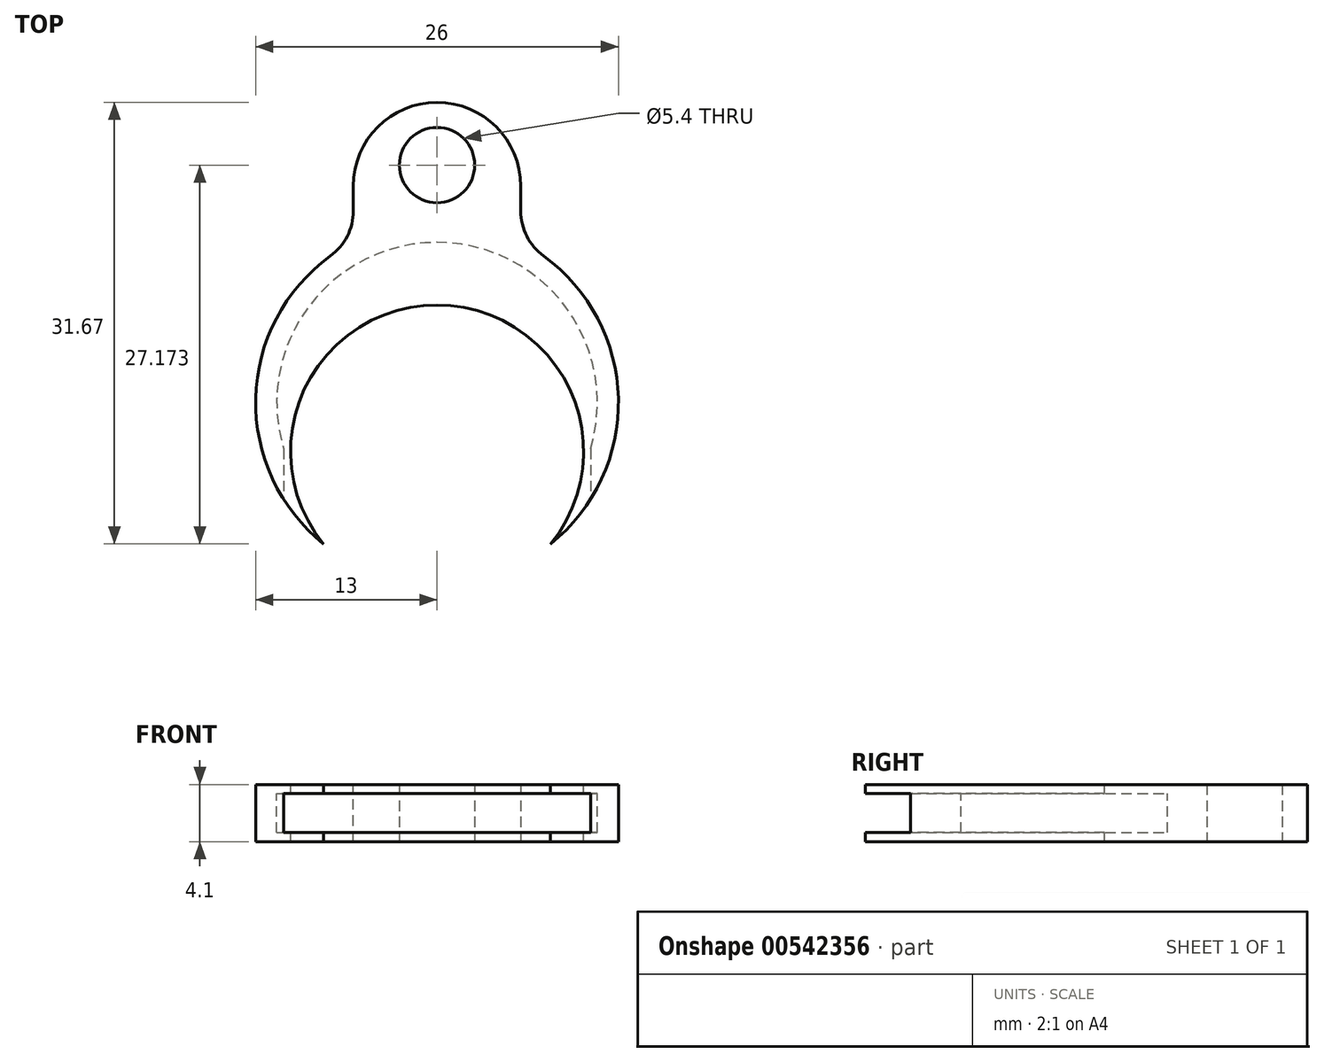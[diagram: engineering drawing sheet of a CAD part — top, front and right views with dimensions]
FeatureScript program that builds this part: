
annotation { "Feature Type Name" : "Feature", "Feature Type Description" : "" }
export const myFeature = defineFeature(function(context is Context, id is Id, definition is map)
    precondition{}
    {
        {
            var Q0;
            Q0=qCreatedBy(makeId("Top.planeOp"),FACE);
            var sketch = newSketch(context, id + "F0", { "sketchPlane" : qUnion([Q0])});
            skCircle(sketch, "E0", {"center": v(0, 0) * mm, "radius": 13 * mm});
            skLineSegment(sketch, "E1.bottom", {"start": v(-6, 21.53) * mm, "end": v(6, 21.53) * mm});
            skLineSegment(sketch, "E1.top", {"start": v(-6, 11.53) * mm, "end": v(6, 11.53) * mm});
            skLineSegment(sketch, "E1.left", {"start": v(-6, 21.53) * mm, "end": v(-6, 11.53) * mm});
            skLineSegment(sketch, "E1.right", {"start": v(6, 21.53) * mm, "end": v(6, 11.53) * mm});
            skCircle(sketch, "E2", {"center": v(0, 17.03) * mm, "radius": 2.7 * mm});
            skSolve(sketch);
        }
        {
            var Q0;
            Q0 = qSketchRegion(id + "F0", true);
            extrude(context, id + "F1", {"entities" : qUnion([Q0]), "endBound" : BoundingType.SYMMETRIC, "depth" : 4.1 * mm, "offsetDistance" : 25 * mm});
        }
        {
            var Q0;
            Q0=makeQuery(id+"F1.opExtrude","SWEPT_EDGE",EDGE,{"disambiguationData":[OSD([sQuery(id+"F0.wireOp",EDGE,"E1.bottom"),sQuery(id+"F0.wireOp",EDGE,"E1.left")])]});
            var Q1;
            Q1=makeQuery(id+"F1.opExtrude","SWEPT_EDGE",EDGE,{"disambiguationData":[OSD([sQuery(id+"F0.wireOp",EDGE,"E1.bottom"),sQuery(id+"F0.wireOp",EDGE,"E1.right")])]});
            fillet(context, id + "F2", {"entities" : qUnion([Q0, Q1]), "radius" : 6 * mm, "tangentPropagation" : true, "allowEdgeOverflow" : false});
        }
        {
            var Q0;
            Q0=makeQuery(id+"F1.opExtrude","SWEPT_EDGE",EDGE,{"disambiguationData":[OSD([sQuery(id+"F0.wireOp",EDGE,"E0"),sQuery(id+"F0.wireOp",EDGE,"E1.top"),sQuery(id+"F0.wireOp",EDGE,"E1.right")])]});
            var Q1;
            Q1=makeQuery(id+"F1.opExtrude","SWEPT_EDGE",EDGE,{"disambiguationData":[OSD([sQuery(id+"F0.wireOp",EDGE,"E0"),sQuery(id+"F0.wireOp",EDGE,"E1.top"),sQuery(id+"F0.wireOp",EDGE,"E1.left")])]});
            fillet(context, id + "F3", {"entities" : qUnion([Q0, Q1]), "radius" : 4 * mm, "tangentPropagation" : true, "allowEdgeOverflow" : false});
        }
        {
            var Q0;
            Q0=makeQuery(id+"F1.opExtrude","CAP_FACE",FACE,{"disambiguationData":[OSD([sQuery(id+"F0.wireOp",EDGE,"E0"),sQuery(id+"F0.wireOp",EDGE,"E1.bottom"),sQuery(id+"F0.wireOp",EDGE,"E1.left"),sQuery(id+"F0.wireOp",EDGE,"E1.right"),sQuery(id+"F0.wireOp",EDGE,"E2")])],"isStart":false});
            var sketch = newSketch(context, id + "F4", { "sketchPlane" : qUnion([Q0])});
            skCircle(sketch, "E3", {"center": v(0, -3.5) * mm, "radius": 10.5 * mm});
            skSolve(sketch);
        }
        {
            var Q0;
            Q0 = qSketchRegion(id + "F4", true);
            extrude(context, id + "F5", {"entities" : qUnion([Q0]), "operationType" : NewBodyOperationType.REMOVE, "endBound" : BoundingType.THROUGH_ALL, "oppositeDirection" : true, "depth" : 25 * mm, "offsetDistance" : 25 * mm});
        }
        {
            var Q0;
            Q0=qCreatedBy(makeId("Top.planeOp"),FACE);
            var sketch = newSketch(context, id + "F6", { "sketchPlane" : qUnion([Q0])});
            skCircle(sketch, "E4", {"center": v(0, 0) * mm, "radius": 11.49 * mm});
            skLineSegment(sketch, "E5.bottom", {"start": v(-11, -3.31) * mm, "end": v(11, -3.31) * mm});
            skLineSegment(sketch, "E5.top", {"start": v(-11, -30.77) * mm, "end": v(11, -30.77) * mm});
            skLineSegment(sketch, "E5.left", {"start": v(-11, -3.31) * mm, "end": v(-11, -30.77) * mm});
            skLineSegment(sketch, "E5.right", {"start": v(11, -3.31) * mm, "end": v(11, -30.77) * mm});
            skSolve(sketch);
        }
        {
            var Q0;
            Q0 = qSketchRegion(id + "F6", true);
            extrude(context, id + "F7", {"entities" : qUnion([Q0]), "operationType" : NewBodyOperationType.REMOVE, "endBound" : BoundingType.SYMMETRIC, "oppositeDirection" : true, "depth" : 2.8 * mm, "offsetDistance" : 25 * mm});
        }
    });
